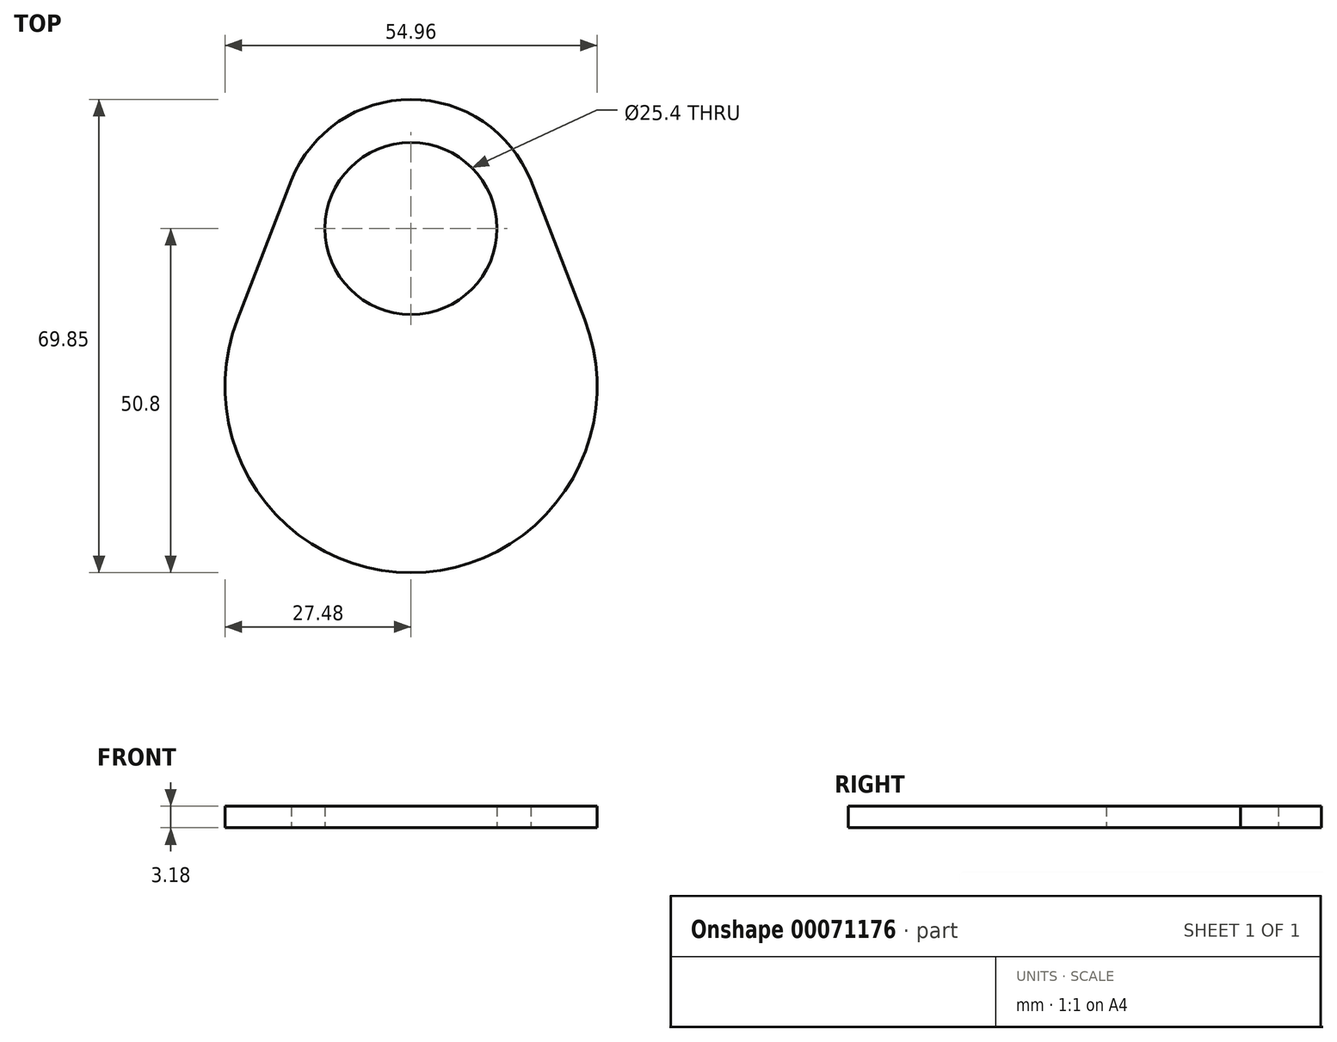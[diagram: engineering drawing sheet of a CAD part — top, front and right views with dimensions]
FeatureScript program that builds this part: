
annotation { "Feature Type Name" : "Feature", "Feature Type Description" : "" }
export const myFeature = defineFeature(function(context is Context, id is Id, definition is map)
    precondition{}
    {
        {
            var Q0;
            Q0=qCreatedBy(makeId("Top.planeOp"),FACE);
            var sketch = newSketch(context, id + "F0", { "sketchPlane" : qUnion([Q0])});
            skCircle(sketch, "E0", {"center": v(0, 0) * mm, "radius": 12.7 * mm});
            skArc(sketch, "E1", {"start": v(17.85, 6.65) * mm, "mid": v(0, 19.05) * mm, "end": v(-17.85, 6.65) * mm});
            skArc(sketch, "E2", {"start": v(-25.62, -13.4) * mm, "mid": v(0, -50.8) * mm, "end": v(25.62, -13.4) * mm});
            skLineSegment(sketch, "E3", {"start": v(17.67, 7.12) * mm, "end": v(25.62, -13.4) * mm});
            skLineSegment(sketch, "E4.MirrorCS", {"start": v(-17.67, 7.12) * mm, "end": v(-25.62, -13.4) * mm});
            skSolve(sketch);
        }
        {
            var Q0;
            Q0=makeQuery(id+"F0.imprint","IMPRINT",FACE,{"disambiguationData":[TD([[makeQuery(id+"F0.imprint","IMPRINT",EDGE,{"derivedFrom":sQuery(id+"F0.wireOp",EDGE,"E0")}),-1.0]])]});
            extrude(context, id + "F1", {"entities" : qUnion([Q0]), "depth" : 3.17 * mm});
        }
    });
